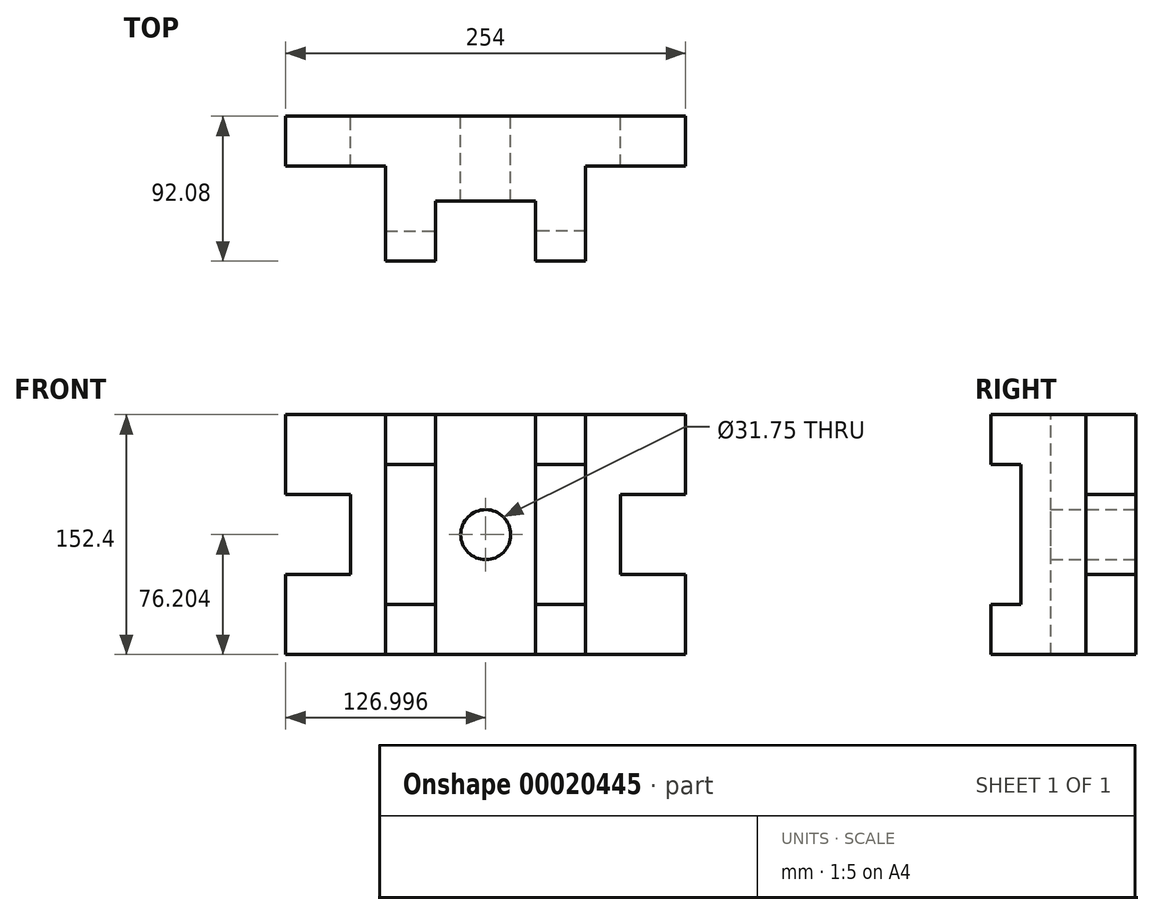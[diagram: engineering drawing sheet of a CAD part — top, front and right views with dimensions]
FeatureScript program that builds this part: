
annotation { "Feature Type Name" : "Feature", "Feature Type Description" : "" }
export const myFeature = defineFeature(function(context is Context, id is Id, definition is map)
    precondition{}
    {
        {
            var Q0;
            Q0=qCreatedBy(makeId("Front.planeOp"),FACE);
            var sketch = newSketch(context, id + "F0", { "sketchPlane" : qUnion([Q0])});
            skLineSegment(sketch, "E0.bottom", {"start": v(-85.4, 9.06) * mm, "end": v(-15.55, 9.06) * mm});
            skLineSegment(sketch, "E0.top", {"start": v(-126.67, -67.14) * mm, "end": v(0.33, -67.14) * mm});
            skLineSegment(sketch, "E0.left", {"start": v(-126.67, -16.34) * mm, "end": v(-126.67, -67.14) * mm});
            skLineSegment(sketch, "E0.right", {"start": v(0.33, -6.81) * mm, "end": v(0.33, -67.14) * mm});
            skArc(sketch, "E1", {"start": v(-15.55, 9.06) * mm, "mid": v(-10.9, -2.16) * mm, "end": v(0.33, -6.81) * mm});
            skPoint(sketch, "E2", {"position": v(-126.67, -16.34) * mm});
            skLineSegment(sketch, "E3", {"start": v(-126.67, -16.34) * mm, "end": v(-85.4, -16.34) * mm});
            skLineSegment(sketch, "E4", {"start": v(-85.4, -16.34) * mm, "end": v(-85.4, 9.06) * mm});
            skLineSegment(sketch, "E5", {"start": v(-63.17, -67.14) * mm, "end": v(-63.17, 9.06) * mm});
            skLineSegment(sketch, "E6", {"start": v(-63.17, -35.39) * mm, "end": v(-31.42, -35.39) * mm});
            skLineSegment(sketch, "E7", {"start": v(-31.42, -35.39) * mm, "end": v(-31.42, -67.14) * mm});
            skLineSegment(sketch, "E8", {"start": v(-31.42, -35.39) * mm, "end": v(-31.42, 9.06) * mm});
            skSolve(sketch);
        }
        {
            var Q0;
            {var subQ5=sQuery(id+"F0.wireOp",EDGE,"E0.left");Q0=makeQuery(id+"F0.imprint","IMPRINT",FACE,{"disambiguationData":[TD([[makeQuery(id+"F0.imprint","IMPRINT",EDGE,{"derivedFrom":subQ5}),1.0]])]});}
            extrude(context, id + "F1", {"entities" : qUnion([Q0]), "depth" : 31.75 * mm});
        }
        {
            var Q0;
            {var subQ1=sQuery(id+"F0.wireOp",EDGE,"E6");Q0=makeQuery(id+"F0.imprint","IMPRINT",FACE,{"disambiguationData":[TD([[makeQuery(id+"F0.imprint","IMPRINT",EDGE,{"derivedFrom":subQ1}),-1.0]])]});}
            extrude(context, id + "F2", {"entities" : qUnion([Q0]), "operationType" : NewBodyOperationType.ADD, "depth" : 92.07 * mm});
        }
        {
            var Q0;
            {var subQ1=sQuery(id+"F0.wireOp",EDGE,"E6");Q0=makeQuery(id+"F0.imprint","IMPRINT",FACE,{"disambiguationData":[TD([[makeQuery(id+"F0.imprint","IMPRINT",EDGE,{"derivedFrom":subQ1}),1.0]])]});}
            extrude(context, id + "F3", {"entities" : qUnion([Q0]), "operationType" : NewBodyOperationType.ADD, "depth" : 73.02 * mm});
        }
        {
            var Q0;
            {var subQ3=sQuery(id+"F0.wireOp",EDGE,"E0.right");Q0=makeQuery(id+"F0.imprint","IMPRINT",FACE,{"disambiguationData":[TD([[makeQuery(id+"F0.imprint","IMPRINT",EDGE,{"derivedFrom":subQ3}),-1.0]])]});}
            extrude(context, id + "F4", {"entities" : qUnion([Q0]), "operationType" : NewBodyOperationType.ADD, "depth" : 53.97 * mm});
        }
        {
            var Q0;
            Q0=makeQuery(id+"F1.opExtrude","SWEPT_BODY",BODY,{"disambiguationData":[OSD([sQuery(id+"F0.wireOp",EDGE,"E0.bottom"),sQuery(id+"F0.wireOp",EDGE,"E0.top"),sQuery(id+"F0.wireOp",EDGE,"E0.left"),sQuery(id+"F0.wireOp",EDGE,"E3"),sQuery(id+"F0.wireOp",EDGE,"E4"),sQuery(id+"F0.wireOp",EDGE,"E5")])]});
            var Q1;
            Q1=makeQuery(id+"F4.opExtrude","SWEPT_FACE",FACE,{"disambiguationData":[OSD([sQuery(id+"F0.wireOp",EDGE,"E0.right")])]});
            mirror(context, id + "F5", {"operationType" : NewBodyOperationType.ADD, "entities" : qUnion([Q0]), "mirrorPlane" : qUnion([Q1])});
        }
        {
            var Q0;
            Q0=makeQuery(id+"F1.opExtrude","SWEPT_BODY",BODY,{"disambiguationData":[OSD([sQuery(id+"F0.wireOp",EDGE,"E0.bottom"),sQuery(id+"F0.wireOp",EDGE,"E0.top"),sQuery(id+"F0.wireOp",EDGE,"E0.left"),sQuery(id+"F0.wireOp",EDGE,"E3"),sQuery(id+"F0.wireOp",EDGE,"E4"),sQuery(id+"F0.wireOp",EDGE,"E5")])]});
            var Q1;
            {var subQ0=sQuery(id+"F0.wireOp",EDGE,"E0.bottom");Q1=makeQuery(id+"F5.opPattern","COPY",FACE,{"derivedFrom":makeQuery(id+"F4.boolean.opBoolean","MERGE",FACE,{"derivedFrom":[makeQuery(id+"F3.boolean.opBoolean","MERGE",FACE,{"derivedFrom":[makeQuery(id+"F1.opExtrude","SWEPT_FACE",FACE,{"disambiguationData":[OSD([subQ0])]}),makeQuery(id+"F3.opExtrude","SWEPT_FACE",FACE,{"disambiguationData":[OSD([subQ0])]})]}),makeQuery(id+"F4.opExtrude","SWEPT_FACE",FACE,{"disambiguationData":[OSD([subQ0])]})]}),"instanceName":"1"});}
            mirror(context, id + "F6", {"operationType" : NewBodyOperationType.ADD, "entities" : qUnion([Q0]), "mirrorPlane" : qUnion([Q1])});
        }
    });
